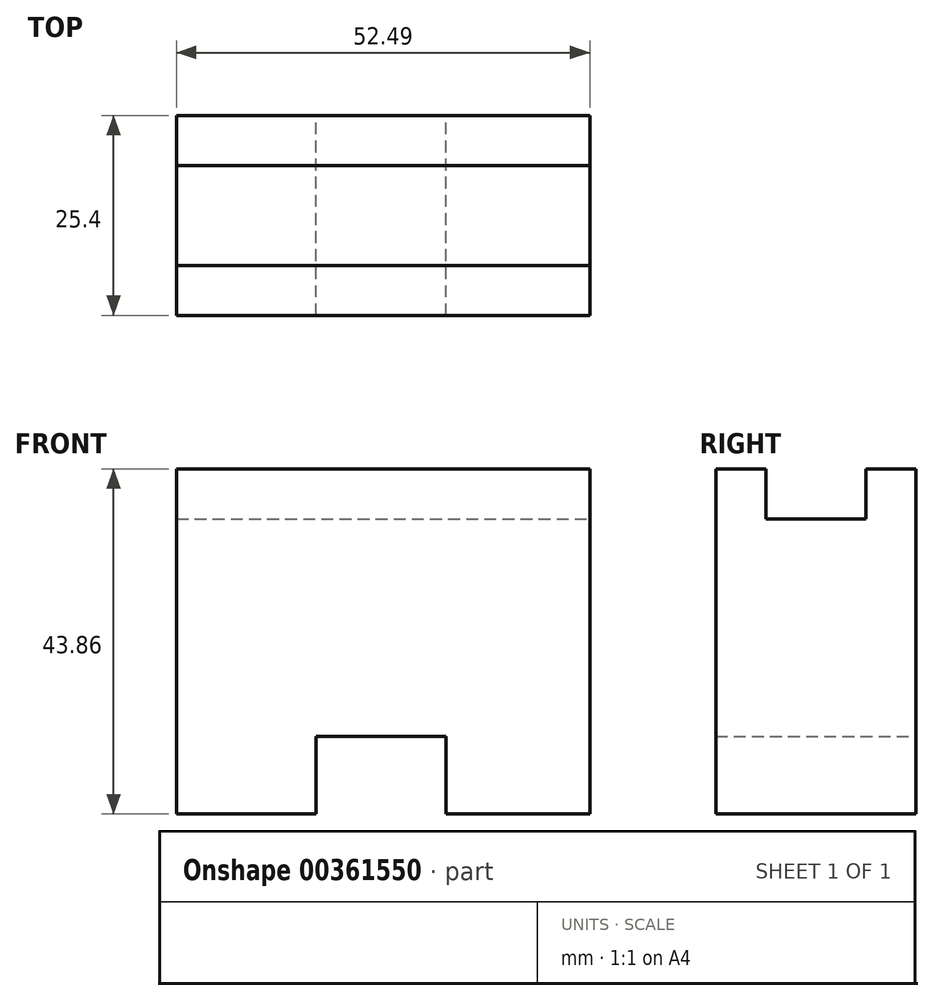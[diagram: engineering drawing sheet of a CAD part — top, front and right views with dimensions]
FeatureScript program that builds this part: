
annotation { "Feature Type Name" : "Feature", "Feature Type Description" : "" }
export const myFeature = defineFeature(function(context is Context, id is Id, definition is map)
    precondition{}
    {
        {
            var Q0;
            Q0=qCreatedBy(makeId("Front.planeOp"),FACE);
            var sketch = newSketch(context, id + "F0", { "sketchPlane" : qUnion([Q0])});
            skLineSegment(sketch, "E0", {"start": v(4.56, 0) * mm, "end": v(4.56, 37.5) * mm});
            skLineSegment(sketch, "E1", {"start": v(4.56, 37.5) * mm, "end": v(57.05, 37.5) * mm});
            skLineSegment(sketch, "E2", {"start": v(57.05, 37.5) * mm, "end": v(57.05, 0) * mm});
            skLineSegment(sketch, "E3", {"start": v(57.05, 0) * mm, "end": v(38.8, 0) * mm});
            skLineSegment(sketch, "E4", {"start": v(38.8, 0) * mm, "end": v(38.8, 9.84) * mm});
            skLineSegment(sketch, "E5", {"start": v(38.8, 9.84) * mm, "end": v(22.25, 9.84) * mm});
            skLineSegment(sketch, "E6", {"start": v(22.25, 9.84) * mm, "end": v(22.25, 0) * mm});
            skLineSegment(sketch, "E7", {"start": v(22.25, 0) * mm, "end": v(4.56, 0) * mm});
            skSolve(sketch);
        }
        {
            var Q0;
            Q0=makeQuery(id+"F0.imprint","IMPRINT",FACE,{"disambiguationData":[TD([[makeQuery(id+"F0.imprint","IMPRINT",EDGE,{"derivedFrom":sQuery(id+"F0.wireOp",EDGE,"E0")}),-1.0]])]});
            extrude(context, id + "F1", {"entities" : qUnion([Q0]), "depth" : 25.4 * mm});
        }
        {
            var Q0;
            Q0=makeQuery(id+"F1.opExtrude","SWEPT_FACE",FACE,{"disambiguationData":[OSD([sQuery(id+"F0.wireOp",EDGE,"E1")])]});
            var sketch = newSketch(context, id + "F2", { "sketchPlane" : qUnion([Q0])});
            skLineSegment(sketch, "E8", {"start": v(4.56, 0) * mm, "end": v(4.56, -6.35) * mm});
            skLineSegment(sketch, "E9", {"start": v(4.56, -6.35) * mm, "end": v(57.05, -6.35) * mm});
            skLineSegment(sketch, "E10", {"start": v(57.05, -6.35) * mm, "end": v(57.05, 0) * mm});
            skLineSegment(sketch, "E11", {"start": v(57.05, 0) * mm, "end": v(4.56, 0) * mm});
            skSolve(sketch);
        }
        {
            var Q0;
            Q0=makeQuery(id+"F2.imprint","IMPRINT",FACE,{"disambiguationData":[TD([[makeQuery(id+"F2.imprint","IMPRINT",EDGE,{"derivedFrom":sQuery(id+"F2.wireOp",EDGE,"E8")}),-1.0]])]});
            extrude(context, id + "F3", {"entities" : qUnion([Q0]), "operationType" : NewBodyOperationType.ADD, "depth" : 6.35 * mm});
        }
        {
            var Q0;
            Q0=makeQuery(id+"F1.opExtrude","SWEPT_FACE",FACE,{"disambiguationData":[OSD([sQuery(id+"F0.wireOp",EDGE,"E1")])]});
            var sketch = newSketch(context, id + "F4", { "sketchPlane" : qUnion([Q0])});
            skLineSegment(sketch, "E12", {"start": v(4.56, -19.05) * mm, "end": v(4.56, -25.4) * mm});
            skLineSegment(sketch, "E13", {"start": v(4.56, -25.4) * mm, "end": v(57.05, -25.4) * mm});
            skLineSegment(sketch, "E14", {"start": v(4.56, -19.05) * mm, "end": v(57.05, -19.05) * mm});
            skLineSegment(sketch, "E15", {"start": v(57.05, -19.05) * mm, "end": v(57.05, -25.4) * mm});
            skSolve(sketch);
        }
        {
            var Q0;
            Q0=makeQuery(id+"F4.imprint","IMPRINT",FACE,{"disambiguationData":[TD([[makeQuery(id+"F4.imprint","IMPRINT",EDGE,{"derivedFrom":sQuery(id+"F4.wireOp",EDGE,"E12")}),-1.0]])]});
            extrude(context, id + "F5", {"entities" : qUnion([Q0]), "operationType" : NewBodyOperationType.ADD, "depth" : 6.35 * mm});
        }
    });
